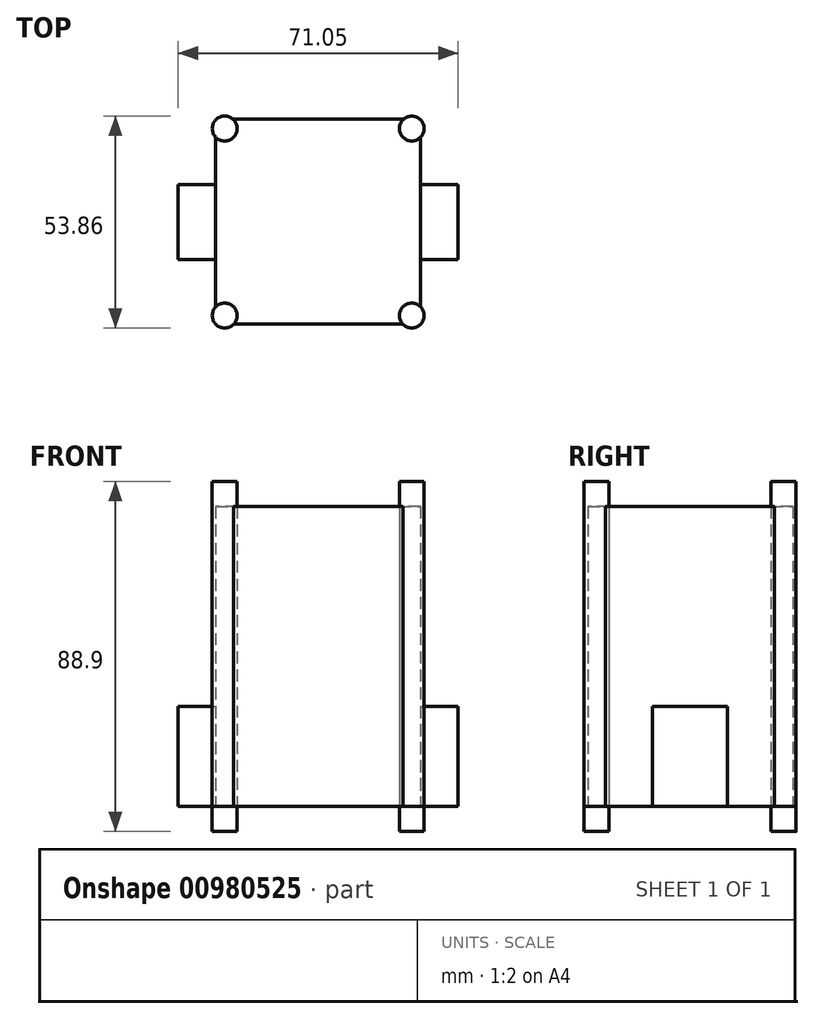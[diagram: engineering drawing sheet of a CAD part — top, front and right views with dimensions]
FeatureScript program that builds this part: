
annotation { "Feature Type Name" : "Feature", "Feature Type Description" : "" }
export const myFeature = defineFeature(function(context is Context, id is Id, definition is map)
    precondition{}
    {
        {
            var Q0;
            Q0=qCreatedBy(makeId("Top.planeOp"),FACE);
            var sketch = newSketch(context, id + "F0", { "sketchPlane" : qUnion([Q0])});
            skCircle(sketch, "E0", {"center": v(-17.92, 20.55) * mm, "radius": 3.17 * mm});
            skCircle(sketch, "E1", {"center": v(-17.92, -26.97) * mm, "radius": 3.17 * mm});
            skCircle(sketch, "E2", {"center": v(29.6, -26.97) * mm, "radius": 3.17 * mm});
            skCircle(sketch, "E3", {"center": v(29.6, 20.55) * mm, "radius": 3.16 * mm});
            skLineSegment(sketch, "E4", {"start": v(-20.2, 18.35) * mm, "end": v(-20.2, -24.76) * mm});
            skLineSegment(sketch, "E5", {"start": v(-15.86, 22.96) * mm, "end": v(27.55, 22.96) * mm});
            skLineSegment(sketch, "E6", {"start": v(31.8, -24.7) * mm, "end": v(31.8, 18.3) * mm});
            skLineSegment(sketch, "E7", {"start": v(-15.64, -29.16) * mm, "end": v(27.31, -29.16) * mm});
            skLineSegment(sketch, "E8.bottom", {"start": v(-29.72, 6.32) * mm, "end": v(-20.2, 6.32) * mm});
            skLineSegment(sketch, "E8.top", {"start": v(-29.72, -12.73) * mm, "end": v(-20.2, -12.73) * mm});
            skLineSegment(sketch, "E8.left", {"start": v(-29.72, 6.32) * mm, "end": v(-29.72, -12.73) * mm});
            skLineSegment(sketch, "E8.right", {"start": v(-20.2, 6.32) * mm, "end": v(-20.2, -12.73) * mm});
            skLineSegment(sketch, "E9.bottom", {"start": v(31.8, 6.33) * mm, "end": v(41.33, 6.33) * mm});
            skLineSegment(sketch, "E9.top", {"start": v(31.8, -12.72) * mm, "end": v(41.33, -12.72) * mm});
            skLineSegment(sketch, "E9.left", {"start": v(31.8, 6.33) * mm, "end": v(31.8, -12.72) * mm});
            skLineSegment(sketch, "E9.right", {"start": v(41.33, 6.33) * mm, "end": v(41.33, -12.72) * mm});
            skSolve(sketch);
        }
        {
            var Q0;
            {var subQ0=sQuery(id+"F0.wireOp",EDGE,"E0");var subQ1=makeQuery(id+"F0.imprint","INTERSECT",VERTEX,{"derivedFrom":[subQ0,sQuery(id+"F0.wireOp",EDGE,"E4")]});Q0=makeQuery(id+"F0.imprint","IMPRINT",FACE,{"disambiguationData":[TD([[makeQuery(id+"F0.imprint","IMPRINT",EDGE,{"disambiguationData":[TD([[subQ1,1.0]])],"derivedFrom":subQ0}),1.0]])]});}
            var Q1;
            {var subQ0=sQuery(id+"F0.wireOp",EDGE,"E3");var subQ1=makeQuery(id+"F0.imprint","INTERSECT",VERTEX,{"derivedFrom":[subQ0,sQuery(id+"F0.wireOp",EDGE,"E5")]});Q1=makeQuery(id+"F0.imprint","IMPRINT",FACE,{"disambiguationData":[TD([[makeQuery(id+"F0.imprint","IMPRINT",EDGE,{"disambiguationData":[TD([[subQ1,-1.0]])],"derivedFrom":subQ0}),1.0]])]});}
            var Q2;
            {var subQ0=sQuery(id+"F0.wireOp",EDGE,"E2");var subQ1=makeQuery(id+"F0.imprint","INTERSECT",VERTEX,{"derivedFrom":[subQ0,sQuery(id+"F0.wireOp",EDGE,"E6")]});Q2=makeQuery(id+"F0.imprint","IMPRINT",FACE,{"disambiguationData":[TD([[makeQuery(id+"F0.imprint","IMPRINT",EDGE,{"disambiguationData":[TD([[subQ1,-1.0]])],"derivedFrom":subQ0}),1.0]])]});}
            var Q3;
            {var subQ0=sQuery(id+"F0.wireOp",EDGE,"E1");var subQ1=makeQuery(id+"F0.imprint","INTERSECT",VERTEX,{"derivedFrom":[subQ0,sQuery(id+"F0.wireOp",EDGE,"E4")]});Q3=makeQuery(id+"F0.imprint","IMPRINT",FACE,{"disambiguationData":[TD([[makeQuery(id+"F0.imprint","IMPRINT",EDGE,{"disambiguationData":[TD([[subQ1,-1.0]])],"derivedFrom":subQ0}),1.0]])]});}
            extrude(context, id + "F1", {"entities" : qUnion([Q0, Q1, Q2, Q3]), "depth" : 82.55 * mm, "offsetDistance" : 25.4 * mm});
        }
        {
            var Q0;
            {var subQ5=sQuery(id+"F0.wireOp",EDGE,"E5");Q0=makeQuery(id+"F0.imprint","IMPRINT",FACE,{"disambiguationData":[TD([[makeQuery(id+"F0.imprint","IMPRINT",EDGE,{"derivedFrom":subQ5}),-1.0]])]});}
            extrude(context, id + "F2", {"entities" : qUnion([Q0]), "depth" : 76.2 * mm, "offsetDistance" : 25.4 * mm});
        }
        {
            var Q0;
            Q0=makeQuery(id+"F0.imprint","IMPRINT",FACE,{"disambiguationData":[TD([[makeQuery(id+"F0.imprint","IMPRINT",EDGE,{"derivedFrom":sQuery(id+"F0.wireOp",EDGE,"E8.bottom")}),-1.0]])]});
            var Q1;
            Q1=makeQuery(id+"F0.imprint","IMPRINT",FACE,{"disambiguationData":[TD([[makeQuery(id+"F0.imprint","IMPRINT",EDGE,{"derivedFrom":sQuery(id+"F0.wireOp",EDGE,"E9.bottom")}),-1.0]])]});
            extrude(context, id + "F3", {"entities" : qUnion([Q0, Q1]), "operationType" : NewBodyOperationType.ADD, "depth" : 25.4 * mm, "offsetDistance" : 25.4 * mm});
        }
        {
            var Q0;
            {var subQ0=sQuery(id+"F0.wireOp",EDGE,"E1");var subQ1=makeQuery(id+"F0.imprint","INTERSECT",VERTEX,{"derivedFrom":[subQ0,sQuery(id+"F0.wireOp",EDGE,"E4")]});Q0=makeQuery(id+"F0.imprint","IMPRINT",FACE,{"disambiguationData":[TD([[makeQuery(id+"F0.imprint","IMPRINT",EDGE,{"disambiguationData":[TD([[subQ1,-1.0]])],"derivedFrom":subQ0}),1.0]])]});}
            var Q1;
            {var subQ0=sQuery(id+"F0.wireOp",EDGE,"E0");var subQ1=makeQuery(id+"F0.imprint","INTERSECT",VERTEX,{"derivedFrom":[subQ0,sQuery(id+"F0.wireOp",EDGE,"E4")]});Q1=makeQuery(id+"F0.imprint","IMPRINT",FACE,{"disambiguationData":[TD([[makeQuery(id+"F0.imprint","IMPRINT",EDGE,{"disambiguationData":[TD([[subQ1,1.0]])],"derivedFrom":subQ0}),1.0]])]});}
            var Q2;
            {var subQ0=sQuery(id+"F0.wireOp",EDGE,"E3");var subQ1=makeQuery(id+"F0.imprint","INTERSECT",VERTEX,{"derivedFrom":[subQ0,sQuery(id+"F0.wireOp",EDGE,"E5")]});Q2=makeQuery(id+"F0.imprint","IMPRINT",FACE,{"disambiguationData":[TD([[makeQuery(id+"F0.imprint","IMPRINT",EDGE,{"disambiguationData":[TD([[subQ1,-1.0]])],"derivedFrom":subQ0}),1.0]])]});}
            var Q3;
            {var subQ0=sQuery(id+"F0.wireOp",EDGE,"E2");var subQ1=makeQuery(id+"F0.imprint","INTERSECT",VERTEX,{"derivedFrom":[subQ0,sQuery(id+"F0.wireOp",EDGE,"E6")]});Q3=makeQuery(id+"F0.imprint","IMPRINT",FACE,{"disambiguationData":[TD([[makeQuery(id+"F0.imprint","IMPRINT",EDGE,{"disambiguationData":[TD([[subQ1,-1.0]])],"derivedFrom":subQ0}),1.0]])]});}
            extrude(context, id + "F4", {"entities" : qUnion([Q0, Q1, Q2, Q3]), "depth" : 0 * mm, "offsetDistance" : 25.4 * mm, "hasSecondDirection" : true, "secondDirectionOppositeDirection" : true, "secondDirectionDepth" : 6.35 * mm});
        }
    });
